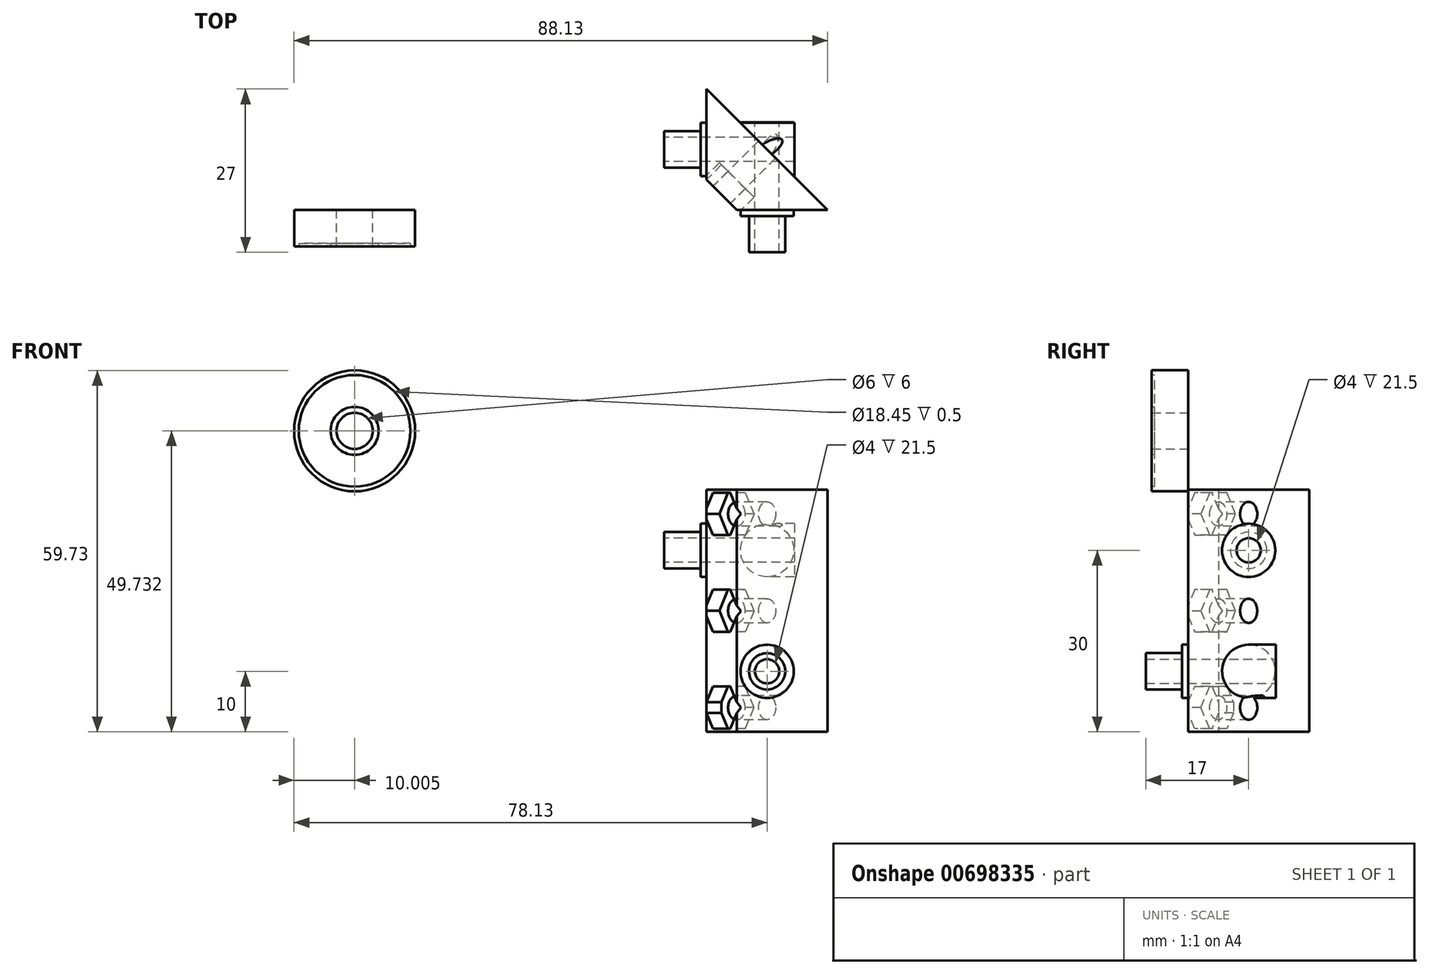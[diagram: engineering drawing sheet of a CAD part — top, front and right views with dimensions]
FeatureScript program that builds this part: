
annotation { "Feature Type Name" : "Feature", "Feature Type Description" : "" }
export const myFeature = defineFeature(function(context is Context, id is Id, definition is map)
    precondition{}
    {
        {
            var Q0;
            Q0=qCreatedBy(makeId("Top.planeOp"),FACE);
            var sketch = newSketch(context, id + "F0", { "sketchPlane" : qUnion([Q0])});
            skLineSegment(sketch, "E0", {"start": v(5, 0) * mm, "end": v(20, 0) * mm});
            skLineSegment(sketch, "E1", {"start": v(0, 5) * mm, "end": v(0, 20) * mm});
            skLineSegment(sketch, "E2", {"start": v(0, 20) * mm, "end": v(20, 0) * mm});
            skLineSegment(sketch, "E3", {"start": v(5, 0) * mm, "end": v(0, 5) * mm});
            skSolve(sketch);
        }
        {
            var Q0;
            Q0 = qSketchRegion(id + "F0", true);
            extrude(context, id + "F1", {"entities" : qUnion([Q0]), "depth" : 40 * mm, "offsetDistance" : 25 * mm});
        }
        {
            var Q0;
            Q0=makeQuery(id+"F1.opExtrude","SWEPT_FACE",FACE,{"disambiguationData":[OSD([sQuery(id+"F0.wireOp",EDGE,"E1")])]});
            var sketch = newSketch(context, id + "F2", { "sketchPlane" : qUnion([Q0])});
            skCircle(sketch, "E4", {"center": v(-10, 30) * mm, "radius": 3 * mm});
            skCircle(sketch, "E5", {"center": v(-10, 30) * mm, "radius": 4.4 * mm});
            skSolve(sketch);
        }
        {
            var Q0;
            Q0=makeQuery(id+"F2.imprint","IMPRINT",FACE,{"disambiguationData":[TD([[makeQuery(id+"F2.imprint","IMPRINT",EDGE,{"derivedFrom":sQuery(id+"F2.wireOp",EDGE,"E4")}),1.0]])]});
            extrude(context, id + "F3", {"entities" : qUnion([Q0]), "operationType" : NewBodyOperationType.ADD, "depth" : 7 * mm, "offsetDistance" : 25 * mm});
        }
        {
            var Q0;
            Q0 = qSketchRegion(id + "F2", true);
            extrude(context, id + "F4", {"entities" : qUnion([Q0]), "operationType" : NewBodyOperationType.ADD, "depth" : 1 * mm, "offsetDistance" : 25 * mm});
        }
        {
            var Q0;
            Q0=makeQuery(id+"F3.opExtrude","CAP_FACE",FACE,{"disambiguationData":[OSD([sQuery(id+"F2.wireOp",EDGE,"E4")])],"isStart":false});
            var sketch = newSketch(context, id + "F5", { "sketchPlane" : qUnion([Q0])});
            skPoint(sketch, "E6", {"position": v(-10, 30) * mm});
            skSolve(sketch);
        }
        {
            var Q0;
            Q0=sQuery(id+"F5.wireOp",VERTEX,"E6");
            var Q1;
            Q1=makeQuery(id+"F1.opExtrude","SWEPT_BODY",BODY,{"disambiguationData":[OSD([sQuery(id+"F0.wireOp",EDGE,"E0"),sQuery(id+"F0.wireOp",EDGE,"E1"),sQuery(id+"F0.wireOp",EDGE,"E2"),sQuery(id+"F0.wireOp",EDGE,"E3")])]});
            hole(context, id + "F6", {"style" : HoleStyle.SIMPLE, "endStyle" : HoleEndStyle.THROUGH, "holeDiameter" : 4 * mm, "majorDiameter" : 5 * mm, "isTappedThrough" : true, "tappedDepth" : 12 * mm, "tapClearance" : 3, "startFromSketch" : true, "locations" : qUnion([Q0]), "scope" : qUnion([Q1])});
        }
        {
            var Q0;
            Q0=makeQuery(id+"F1.opExtrude","SWEPT_FACE",FACE,{"disambiguationData":[OSD([sQuery(id+"F0.wireOp",EDGE,"E0")])]});
            var sketch = newSketch(context, id + "F7", { "sketchPlane" : qUnion([Q0])});
            skCircle(sketch, "E7", {"center": v(10, 10) * mm, "radius": 3 * mm});
            skCircle(sketch, "E8", {"center": v(10, 10) * mm, "radius": 4.4 * mm});
            skSolve(sketch);
        }
        {
            var Q0;
            Q0=makeQuery(id+"F7.imprint","IMPRINT",FACE,{"disambiguationData":[TD([[makeQuery(id+"F7.imprint","IMPRINT",EDGE,{"derivedFrom":sQuery(id+"F7.wireOp",EDGE,"E7")}),1.0]])]});
            extrude(context, id + "F8", {"entities" : qUnion([Q0]), "operationType" : NewBodyOperationType.ADD, "depth" : 7 * mm, "offsetDistance" : 25 * mm});
        }
        {
            var Q0;
            Q0 = qSketchRegion(id + "F7", true);
            var Q1;
            Q1=makeQuery(id+"F7.imprint","IMPRINT",FACE,{"disambiguationData":[TD([[makeQuery(id+"F7.imprint","IMPRINT",EDGE,{"derivedFrom":sQuery(id+"F7.wireOp",EDGE,"E7")}),-1.0]])]});
            extrude(context, id + "F9", {"entities" : qUnion([Q0, Q1]), "operationType" : NewBodyOperationType.ADD, "depth" : 1 * mm, "offsetDistance" : 25 * mm});
        }
        {
            var Q0;
            Q0=sQuery(id+"F7.wireOp",VERTEX,"E7.center");
            var Q1;
            Q1=makeQuery(id+"F1.opExtrude","SWEPT_BODY",BODY,{"disambiguationData":[OSD([sQuery(id+"F0.wireOp",EDGE,"E0"),sQuery(id+"F0.wireOp",EDGE,"E1"),sQuery(id+"F0.wireOp",EDGE,"E2"),sQuery(id+"F0.wireOp",EDGE,"E3")])]});
            hole(context, id + "F10", {"style" : HoleStyle.SIMPLE, "endStyle" : HoleEndStyle.THROUGH, "oppositeDirection" : true, "holeDiameter" : 4 * mm, "majorDiameter" : 5 * mm, "isTappedThrough" : true, "tappedDepth" : 12 * mm, "tapClearance" : 3, "startFromSketch" : true, "locations" : qUnion([Q0]), "scope" : qUnion([Q1])});
        }
        {
            var Q0;
            Q0=sQuery(id+"F7.wireOp",VERTEX,"E7.center");
            var Q1;
            Q1=makeQuery(id+"F1.opExtrude","SWEPT_BODY",BODY,{"disambiguationData":[OSD([sQuery(id+"F0.wireOp",EDGE,"E0"),sQuery(id+"F0.wireOp",EDGE,"E1"),sQuery(id+"F0.wireOp",EDGE,"E2"),sQuery(id+"F0.wireOp",EDGE,"E3")])]});
            hole(context, id + "F11", {"style" : HoleStyle.SIMPLE, "endStyle" : HoleEndStyle.THROUGH, "holeDiameter" : 4 * mm, "majorDiameter" : 5 * mm, "isTappedThrough" : true, "tappedDepth" : 12 * mm, "tapClearance" : 3, "startFromSketch" : true, "locations" : qUnion([Q0]), "scope" : qUnion([Q1])});
        }
        {
            var Q0;
            Q0=makeQuery(id+"F9.opExtrude","CAP_FACE",FACE,{"disambiguationData":[OSD([sQuery(id+"F7.wireOp",EDGE,"E7"),sQuery(id+"F7.wireOp",EDGE,"E8")])],"isStart":false});
            extrude(context, id + "F12", {"entities" : qUnion([Q0]), "operationType" : NewBodyOperationType.ADD, "oppositeDirection" : true, "depth" : 15.5 * mm, "offsetDistance" : 25 * mm});
        }
        {
            var Q0;
            Q0=makeQuery(id+"F8.opExtrude","CAP_FACE",FACE,{"disambiguationData":[OSD([sQuery(id+"F7.wireOp",EDGE,"E7")])],"isStart":false});
            extrude(context, id + "F13", {"entities" : qUnion([Q0]), "operationType" : NewBodyOperationType.ADD, "oppositeDirection" : true, "depth" : 21.5 * mm, "offsetDistance" : 25 * mm});
        }
        {
            var Q0;
            Q0=makeQuery(id+"F4.opExtrude","CAP_FACE",FACE,{"disambiguationData":[OSD([sQuery(id+"F2.wireOp",EDGE,"E4"),sQuery(id+"F2.wireOp",EDGE,"E5")])],"isStart":false});
            extrude(context, id + "F14", {"entities" : qUnion([Q0]), "operationType" : NewBodyOperationType.ADD, "oppositeDirection" : true, "depth" : 15.5 * mm, "offsetDistance" : 25 * mm});
        }
        {
            var Q0;
            Q0=makeQuery(id+"F3.opExtrude","CAP_FACE",FACE,{"disambiguationData":[OSD([sQuery(id+"F2.wireOp",EDGE,"E4")])],"isStart":false});
            extrude(context, id + "F15", {"entities" : qUnion([Q0]), "operationType" : NewBodyOperationType.ADD, "oppositeDirection" : true, "depth" : 21.5 * mm, "offsetDistance" : 25 * mm});
        }
        {
            var Q0;
            Q0=makeQuery(id+"F1.opExtrude","SWEPT_FACE",FACE,{"disambiguationData":[OSD([sQuery(id+"F0.wireOp",EDGE,"E3")])]});
            var sketch = newSketch(context, id + "F16", { "sketchPlane" : qUnion([Q0])});
            skPoint(sketch, "E9", {"position": v(0, 36) * mm});
            skCircle(sketch, "E10.cCircle", {"center": v(0, 36) * mm, "radius": 3.5 * mm, "construction": true});
            skLineSegment(sketch, "E10.0", {"start": v(2.02, 39.5) * mm, "end": v(4.04, 36) * mm});
            skLineSegment(sketch, "E10.1", {"start": v(4.04, 36) * mm, "end": v(2.02, 32.5) * mm});
            skLineSegment(sketch, "E10.2", {"start": v(2.02, 32.5) * mm, "end": v(-2.02, 32.5) * mm});
            skLineSegment(sketch, "E10.3", {"start": v(-2.02, 32.5) * mm, "end": v(-4.04, 36) * mm});
            skLineSegment(sketch, "E10.4", {"start": v(-4.04, 36) * mm, "end": v(-2.02, 39.5) * mm});
            skLineSegment(sketch, "E10.5", {"start": v(-2.02, 39.5) * mm, "end": v(2.02, 39.5) * mm});
            skPoint(sketch, "E10.0.midPoint", {"position": v(3.03, 37.75) * mm});
            skLineSegment(sketch, "E11", {"start": v(-3.54, 20) * mm, "end": v(3.54, 20) * mm});
            skLineSegment(sketch, "E12.MirrorCS", {"start": v(2.02, 0.5) * mm, "end": v(4.04, 4) * mm});
            skLineSegment(sketch, "E13.MirrorCS", {"start": v(-2.02, 0.5) * mm, "end": v(2.02, 0.5) * mm});
            skLineSegment(sketch, "E14.MirrorCS", {"start": v(-4.04, 4) * mm, "end": v(-2.02, 0.5) * mm});
            skLineSegment(sketch, "E15.MirrorCS", {"start": v(-2.02, 7.5) * mm, "end": v(-4.04, 4) * mm});
            skLineSegment(sketch, "E16.MirrorCS", {"start": v(2.02, 7.5) * mm, "end": v(-2.02, 7.5) * mm});
            skLineSegment(sketch, "E17.MirrorCS", {"start": v(4.04, 4) * mm, "end": v(2.02, 7.5) * mm});
            skCircle(sketch, "E18.MirrorC", {"center": v(0, 4) * mm, "radius": 3.5 * mm, "construction": true});
            skPoint(sketch, "E19.MirrorP", {"position": v(3.03, 2.25) * mm});
            skPoint(sketch, "E20", {"position": v(0, 20) * mm});
            skCircle(sketch, "E21.cCircle", {"center": v(0, 20) * mm, "radius": 3.5 * mm, "construction": true});
            skLineSegment(sketch, "E21.0", {"start": v(2.04, 23.49) * mm, "end": v(4.04, 19.98) * mm});
            skLineSegment(sketch, "E21.1", {"start": v(4.04, 19.98) * mm, "end": v(2, 16.49) * mm});
            skLineSegment(sketch, "E21.2", {"start": v(2, 16.49) * mm, "end": v(-2.04, 16.51) * mm});
            skLineSegment(sketch, "E21.3", {"start": v(-2.04, 16.51) * mm, "end": v(-4.04, 20.02) * mm});
            skLineSegment(sketch, "E21.4", {"start": v(-4.04, 20.02) * mm, "end": v(-2, 23.51) * mm});
            skLineSegment(sketch, "E21.5", {"start": v(-2, 23.51) * mm, "end": v(2.04, 23.49) * mm});
            skPoint(sketch, "E21.0.midPoint", {"position": v(3.04, 21.73) * mm});
            skSolve(sketch);
        }
        {
            var Q0;
            Q0=sQuery(id+"F16.wireOp",VERTEX,"E9");
            var Q1;
            Q1=sQuery(id+"F16.wireOp",VERTEX,"E18.MirrorC.center");
            var Q2;
            Q2=makeQuery(id+"F1.opExtrude","SWEPT_BODY",BODY,{"disambiguationData":[OSD([sQuery(id+"F0.wireOp",EDGE,"E0"),sQuery(id+"F0.wireOp",EDGE,"E1"),sQuery(id+"F0.wireOp",EDGE,"E2"),sQuery(id+"F0.wireOp",EDGE,"E3")])]});
            hole(context, id + "F17", {"style" : HoleStyle.SIMPLE, "endStyle" : HoleEndStyle.THROUGH, "holeDiameter" : 4 * mm, "majorDiameter" : 5 * mm, "isTappedThrough" : true, "tappedDepth" : 12 * mm, "tapClearance" : 3, "startFromSketch" : true, "locations" : qUnion([Q0, Q1]), "scope" : qUnion([Q2])});
        }
        {
            var Q0;
            Q0=sQuery(id+"F16.wireOp",VERTEX,"E20");
            var Q1;
            Q1=makeQuery(id+"F1.opExtrude","SWEPT_BODY",BODY,{"disambiguationData":[OSD([sQuery(id+"F0.wireOp",EDGE,"E0"),sQuery(id+"F0.wireOp",EDGE,"E1"),sQuery(id+"F0.wireOp",EDGE,"E2"),sQuery(id+"F0.wireOp",EDGE,"E3")])]});
            hole(context, id + "F18", {"style" : HoleStyle.SIMPLE, "endStyle" : HoleEndStyle.THROUGH, "holeDiameter" : 4 * mm, "majorDiameter" : 5 * mm, "isTappedThrough" : true, "tappedDepth" : 12 * mm, "tapClearance" : 3, "startFromSketch" : true, "locations" : qUnion([Q0]), "scope" : qUnion([Q1])});
        }
        {
            var Q0;
            {var subQ0=sQuery(id+"F16.wireOp",EDGE,"E10.2");Q0=makeQuery(id+"F16.imprint","IMPRINT",FACE,{"disambiguationData":[TD([[makeQuery(id+"F16.imprint","IMPRINT",EDGE,{"derivedFrom":subQ0}),-1.0]])]});}
            var Q1;
            {var subQ8=sQuery(id+"F16.wireOp",EDGE,"E11");Q1=makeQuery(id+"F16.imprint","IMPRINT",FACE,{"disambiguationData":[TD([[makeQuery(id+"F16.imprint","IMPRINT",EDGE,{"derivedFrom":subQ8}),1.0]])]});}
            var Q2;
            {var subQ8=sQuery(id+"F16.wireOp",EDGE,"E11");Q2=makeQuery(id+"F16.imprint","IMPRINT",FACE,{"disambiguationData":[TD([[makeQuery(id+"F16.imprint","IMPRINT",EDGE,{"derivedFrom":subQ8}),-1.0]])]});}
            var Q3;
            {var subQ1=sQuery(id+"F16.wireOp",EDGE,"E13.MirrorCS");Q3=makeQuery(id+"F16.imprint","IMPRINT",FACE,{"disambiguationData":[TD([[makeQuery(id+"F16.imprint","IMPRINT",EDGE,{"derivedFrom":subQ1}),1.0]])]});}
            var Q4;
            {var subQ0=sQuery(id+"F16.wireOp",EDGE,"E21.4");var subQ1=sQuery(id+"F16.wireOp",EDGE,"E21.3");var subQ2=makeQuery(id+"F16.imprint","INTERSECT",VERTEX,{"derivedFrom":[subQ1,subQ0]});Q4=makeQuery(id+"F16.imprint","IMPRINT",FACE,{"disambiguationData":[TD([[makeQuery(id+"F16.imprint","IMPRINT",EDGE,{"disambiguationData":[TD([[subQ2,1.0]])],"derivedFrom":subQ1}),-1.0]])]});}
            var Q5;
            {var subQ0=sQuery(id+"F16.wireOp",EDGE,"E10.4");var subQ1=sQuery(id+"F16.wireOp",EDGE,"E10.3");var subQ2=makeQuery(id+"F16.imprint","INTERSECT",VERTEX,{"derivedFrom":[subQ1,subQ0]});Q5=makeQuery(id+"F16.imprint","IMPRINT",FACE,{"disambiguationData":[TD([[makeQuery(id+"F16.imprint","IMPRINT",EDGE,{"disambiguationData":[TD([[subQ2,1.0]])],"derivedFrom":subQ1}),-1.0]])]});}
            var Q6;
            {var subQ0=sQuery(id+"F16.wireOp",EDGE,"E10.1");var subQ1=sQuery(id+"F16.wireOp",EDGE,"E10.0");var subQ2=makeQuery(id+"F16.imprint","INTERSECT",VERTEX,{"derivedFrom":[subQ1,subQ0]});Q6=makeQuery(id+"F16.imprint","IMPRINT",FACE,{"disambiguationData":[TD([[makeQuery(id+"F16.imprint","IMPRINT",EDGE,{"disambiguationData":[TD([[subQ2,1.0]])],"derivedFrom":subQ1}),-1.0]])]});}
            var Q7;
            {var subQ0=sQuery(id+"F16.wireOp",EDGE,"E21.1");var subQ1=sQuery(id+"F16.wireOp",EDGE,"E21.0");var subQ2=makeQuery(id+"F16.imprint","INTERSECT",VERTEX,{"derivedFrom":[subQ1,subQ0]});Q7=makeQuery(id+"F16.imprint","IMPRINT",FACE,{"disambiguationData":[TD([[makeQuery(id+"F16.imprint","IMPRINT",EDGE,{"disambiguationData":[TD([[subQ2,1.0]])],"derivedFrom":subQ1}),-1.0]])]});}
            var Q8;
            {var subQ0=sQuery(id+"F16.wireOp",EDGE,"E17.MirrorCS");var subQ1=sQuery(id+"F16.wireOp",EDGE,"E12.MirrorCS");var subQ2=makeQuery(id+"F16.imprint","INTERSECT",VERTEX,{"derivedFrom":[subQ1,subQ0]});Q8=makeQuery(id+"F16.imprint","IMPRINT",FACE,{"disambiguationData":[TD([[makeQuery(id+"F16.imprint","IMPRINT",EDGE,{"disambiguationData":[TD([[subQ2,1.0]])],"derivedFrom":subQ1}),1.0]])]});}
            extrude(context, id + "F19", {"entities" : qUnion([Q0, Q1, Q2, Q3, Q4, Q5, Q6, Q7, Q8]), "operationType" : NewBodyOperationType.REMOVE, "oppositeDirection" : true, "depth" : 3.5 * mm, "offsetDistance" : 25 * mm});
        }
        {
            var Q0;
            Q0=qCreatedBy(makeId("Front.planeOp"),FACE);
            var sketch = newSketch(context, id + "F20", { "sketchPlane" : qUnion([Q0])});
            skCircle(sketch, "E22", {"center": v(-58.13, 49.73) * mm, "radius": 10 * mm});
            skCircle(sketch, "E23", {"center": v(-58.13, 49.73) * mm, "radius": 3 * mm});
            skSolve(sketch);
        }
        {
            var Q0;
            Q0 = qSketchRegion(id + "F20", true);
            extrude(context, id + "F21", {"entities" : qUnion([Q0]), "depth" : 6 * mm, "offsetDistance" : 25 * mm});
        }
        {
            var Q0;
            Q0=makeQuery(id+"F21.opExtrude","CAP_FACE",FACE,{"disambiguationData":[OSD([sQuery(id+"F20.wireOp",EDGE,"E22"),sQuery(id+"F20.wireOp",EDGE,"E23")])],"isStart":false});
            var sketch = newSketch(context, id + "F22", { "sketchPlane" : qUnion([Q0])});
            skCircle(sketch, "E24", {"center": v(-58.13, 49.73) * mm, "radius": 3.96 * mm});
            skCircle(sketch, "E25", {"center": v(-58.13, 49.73) * mm, "radius": 9.22 * mm});
            skSolve(sketch);
        }
        {
            var Q0;
            Q0 = qSketchRegion(id + "F22", true);
            extrude(context, id + "F23", {"entities" : qUnion([Q0]), "operationType" : NewBodyOperationType.REMOVE, "oppositeDirection" : true, "depth" : 0.5 * mm, "offsetDistance" : 25 * mm});
        }
    });
